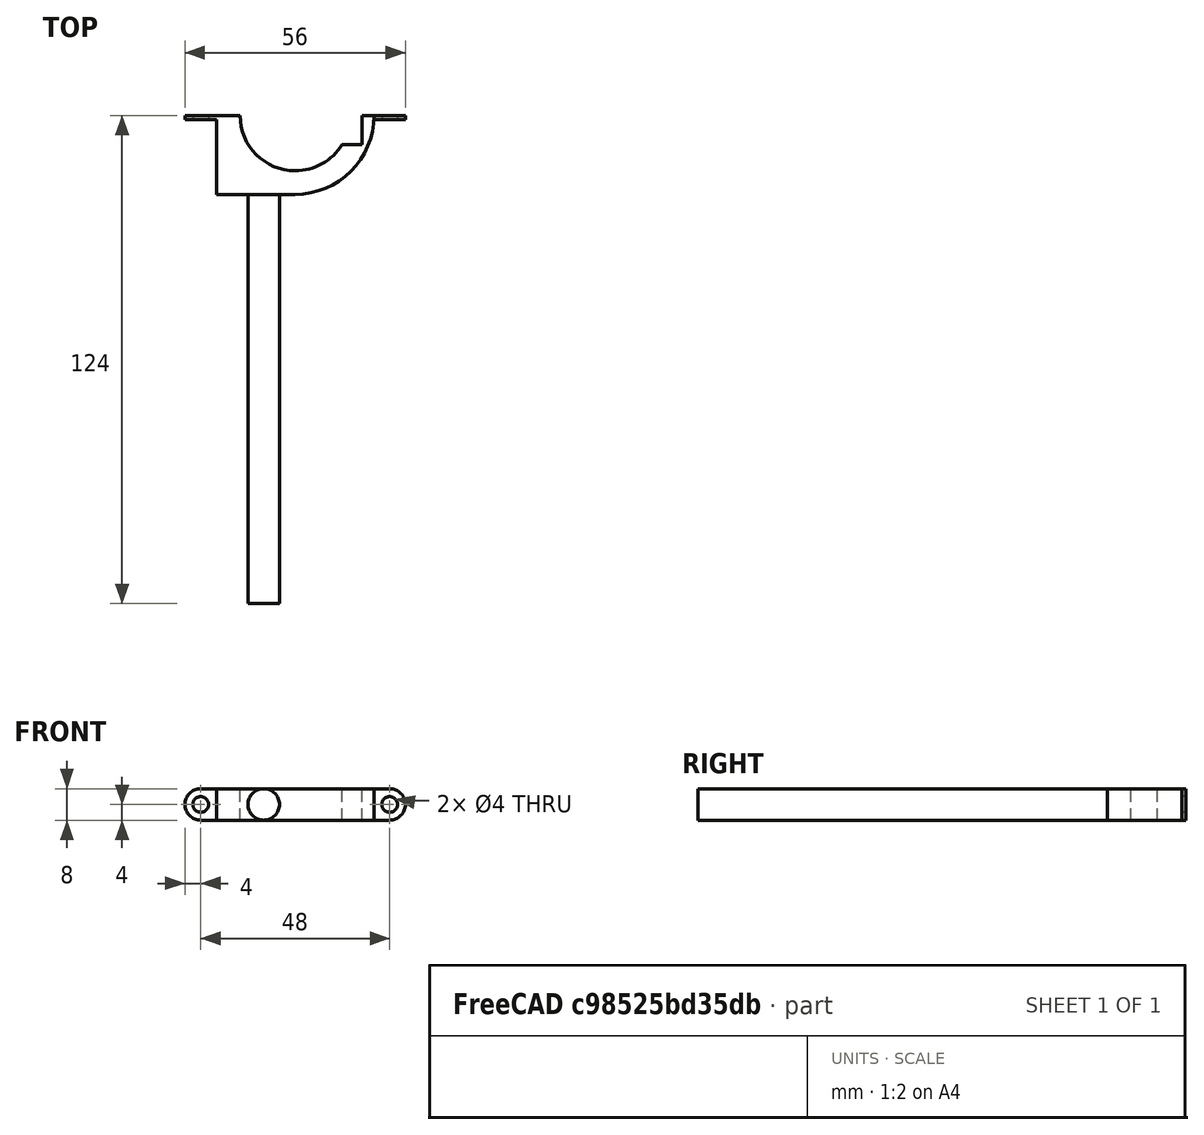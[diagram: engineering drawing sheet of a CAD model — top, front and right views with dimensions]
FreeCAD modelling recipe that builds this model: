
FCSTD DOCUMENT  (FreeCAD 0.16R6706 (Git))
Label: S2H-bottom-motor-holder
License: All rights reserved
LicenseURL: http://en.wikipedia.org/wiki/All_rights_reserved
objects: Part::Cylinder×13, Part::Box×7, Part::Cut×7, Part::MultiFuse×3
note: 30 computed .brp shape members not serialized (recipe doc carries the construction recipe); baked Part::Feature solids carry a one-line shape summary decoded from their .brp

FEATURE [Part::Cylinder] Cylinder008
  Angle = 360
  Height = 110
  Placement = pos=(-8,-14,10) rot=(1,0,0;1.5708rad)
  Radius = 4
FEATURE [Part::Cylinder] Cylinder009
  Angle = 90
  Height = 8
  Placement = pos=(0,0,6) rot=(0,0,-1;1.5708rad)
  Radius = 20
FEATURE [Part::Box] Box004  label="Cube004"
  Height = 8
  Length = 20
  Placement = pos=(0,0,6) rot=(0,0,1;3.14159rad)
  Width = 20
FEATURE [Part::Cylinder] Cylinder010
  Angle = 360
  Height = 1
  Placement = pos=(24,0,10) rot=(1,0,0;1.5708rad)
  Radius = 4
FEATURE [Part::Box] Box005  label="Cube005"
  Height = 8
  Length = 4
  Placement = pos=(20,-1,6) rot=(0,0,1;0rad)
  Width = 1
FEATURE [Part::Cylinder] Cylinder011
  Angle = 360
  Height = 1
  Placement = pos=(-24,0,10) rot=(1,0,0;1.5708rad)
  Radius = 4
FEATURE [Part::Box] Box006  label="Cube006"
  Height = 8
  Length = 4
  Placement = pos=(-24,-1,6) rot=(0,0,1;0rad)
  Width = 1
FEATURE [Part::MultiFuse] Fusion002
  Shapes = -> [Cylinder008,Cylinder009,Box004,Cylinder010,Box005,Cylinder011,Box006]
FEATURE [Part::Cylinder] Cylinder012
  Angle = 360
  Height = 19
  Radius = 14
FEATURE [Part::Cylinder] Cylinder013
  Angle = 360
  Height = 1.5
  Placement = pos=(-8,0,19) rot=(0,0,1;0rad)
  Radius = 4.5
FEATURE [Part::Cylinder] Cylinder014
  Angle = 360
  Height = 8.5
  Placement = pos=(-8,0,20.5) rot=(0,0,1;0rad)
  Radius = 2.5
FEATURE [Part::Cylinder] Cylinder015
  Angle = 360
  Height = 2
  Placement = pos=(0,-17.5,18) rot=(0,0,1;0rad)
  Radius = 2.1
FEATURE [Part::Cylinder] Cylinder016
  Angle = 360
  Height = 2
  Placement = pos=(0,17.5,18) rot=(0,0,1;0rad)
  Radius = 2.1
FEATURE [Part::Cylinder] Cylinder017
  Angle = 360
  Height = 0.75
  Placement = pos=(0,-17.5,18) rot=(0,0,1;0rad)
  Radius = 3.5
FEATURE [Part::Cylinder] Cylinder018
  Angle = 360
  Height = 0.75
  Placement = pos=(0,17.5,18) rot=(0,0,1;0rad)
  Radius = 3.5
FEATURE [Part::Box] Box007  label="Cube007"
  Height = 0.75
  Length = 7
  Placement = pos=(-3.5,-17.5,18) rot=(0,0,1;0rad)
  Width = 35
FEATURE [Part::MultiFuse] Fusion003
  Placement = pos=(0,0,0.25) rot=(0,0,1;0rad)
  Shapes = -> [Cylinder017,Cylinder018,Box007]
FEATURE [Part::Cut] Cut004
  Base = -> Fusion003
  Tool = -> Cylinder015
FEATURE [Part::Cut] Cut005
  Base = -> Cut004
  Tool = -> Cylinder016
FEATURE [Part::Box] Box008  label="Cube008"
  Height = 16.5
  Length = 17
  Placement = pos=(0,-7.3,2.5) rot=(0,0,1;0rad)
  Width = 14.6
FEATURE [Part::Box] Box009  label="Cube009"
  Height = 6
  Length = 1
  Placement = pos=(-6.5,-2.5,23) rot=(0,0,1;0rad)
  Width = 5
FEATURE [Part::Box] Box010  label="Cube010"
  Height = 6
  Length = 1
  Placement = pos=(-10.5,-2.5,23) rot=(0,0,1;0rad)
  Width = 5
FEATURE [Part::Cut] Cut006
  Base = -> Cylinder014
  Tool = -> Box009
FEATURE [Part::Cut] Cut007
  Base = -> Cut006
  Tool = -> Box010
FEATURE [Part::MultiFuse] Fusion004
  Shapes = -> [Cut007,Box008,Cut005,Cylinder013,Cylinder012]
FEATURE [Part::Cut] Cut008
  Base = -> Fusion002
  Placement = pos=(8,0,-10) rot=(0,0,1;0rad)
  Tool = -> Fusion004
FEATURE [Part::Cylinder] Cylinder028
  Angle = 360
  Height = 10
  Placement = pos=(-16,5,0) rot=(1,0,0;1.5708rad)
  Radius = 2
FEATURE [Part::Cylinder] Cylinder029
  Angle = 360
  Height = 10
  Placement = pos=(32,5,0) rot=(1,0,0;1.5708rad)
  Radius = 2
FEATURE [Part::Cut] Cut014
  Base = -> Cut008
  Tool = -> Cylinder028
FEATURE [Part::Cut] Cut015  label="holder"
  Base = -> Cut014
  Tool = -> Cylinder029
